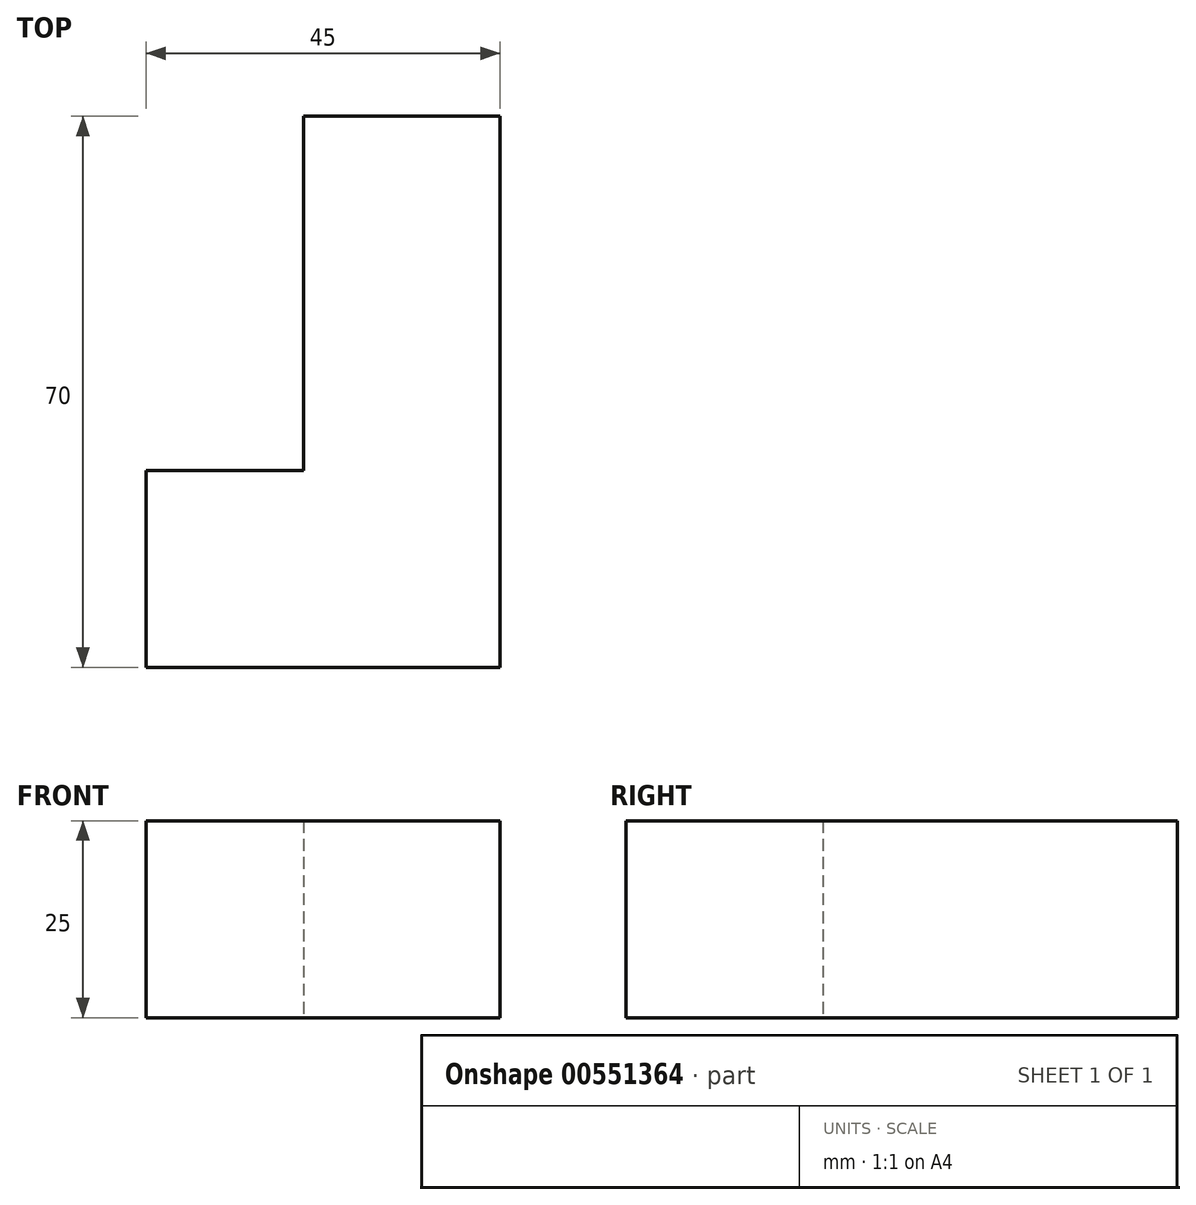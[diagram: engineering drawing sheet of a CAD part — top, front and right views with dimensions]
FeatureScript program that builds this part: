
annotation { "Feature Type Name" : "Feature", "Feature Type Description" : "" }
export const myFeature = defineFeature(function(context is Context, id is Id, definition is map)
    precondition{}
    {
        {
            var Q0;
            Q0=qCreatedBy(makeId("Top.planeOp"),FACE);
            var sketch = newSketch(context, id + "F0", { "sketchPlane" : qUnion([Q0])});
            skLineSegment(sketch, "E0.bottom", {"start": v(-48.5, -39.5) * mm, "end": v(-3.5, -39.5) * mm});
            skLineSegment(sketch, "E0.top", {"start": v(-48.5, -14.5) * mm, "end": v(-3.5, -14.5) * mm});
            skLineSegment(sketch, "E0.left", {"start": v(-48.5, -39.5) * mm, "end": v(-48.5, -14.5) * mm});
            skLineSegment(sketch, "E0.right", {"start": v(-3.5, -39.5) * mm, "end": v(-3.5, -14.5) * mm});
            skLineSegment(sketch, "E1.bottom", {"start": v(-3.5, -14.5) * mm, "end": v(-28.5, -14.5) * mm});
            skLineSegment(sketch, "E1.top", {"start": v(-3.5, 30.5) * mm, "end": v(-28.5, 30.5) * mm});
            skLineSegment(sketch, "E1.left", {"start": v(-3.5, -14.5) * mm, "end": v(-3.5, 30.5) * mm});
            skLineSegment(sketch, "E1.right", {"start": v(-28.5, -14.5) * mm, "end": v(-28.5, 30.5) * mm});
            skSolve(sketch);
        }
        {
            var Q0;
            Q0 = qSketchRegion(id + "F0", true);
            extrude(context, id + "F1", {"entities" : qUnion([Q0]), "depth" : 25 * mm, "offsetDistance" : 25 * mm});
        }
    });
